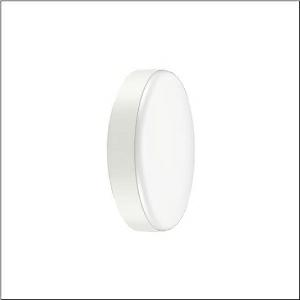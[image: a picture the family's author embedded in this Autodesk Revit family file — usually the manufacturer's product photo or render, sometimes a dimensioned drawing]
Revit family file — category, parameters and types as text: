
# Revit family: round_31_51wc10mb44as
name_source: partatom
category: Lighting Fixtures
units: mm (PartAtom-declared; Revit-internal decimal feet)

## family parameters
Cut with Voids When Loaded = No
Host = Face
Light Source = No
Part Type = Normal
Room Calculation Point = No
Round Connector Dimension = Use Diameter
Shared = No

## types (1)
- --- (1 x LED, 4400 lm, 35.5 W, 4000K)
    Apparent Load = 36 VA
    CIE Flux Codes = 44 75 94 94 100
    Color Rendering = 80
    Color Temperature = 4000K
    Default Elevation = 1800 mm
    Description = Round 31, wall and ceiling luminaire, primary optical cover: cover, of PC, opal, light emission: direct distribution, primary light characteristic: symmetric, installation type: surface-mounted, LED, rated luminous flux: 4.400lm, luminous efficacy: 124lm/W, light colour: 840, colour temperature: 4000K, control gear: ON/OFF Multilumen, with terminal, 3-pole, max. 2.5mm², mains connection: 220..240V, AC, 50/60Hz, rated input power: 35.5W, luminaire housing, of PC, traffic white (RAL 9016), diameter: 480mm, brightness and presence sensor, HF sensor, protection rating (complete): IP65, insulation class (complete): insulation class II (safety insulation), certification: CE, impact resistance: IK10, permissible operating ambient temperature: -20..+40°C, permissible storage temperature: -20..+60°C, packaging unit: 1 piece
    Height = 97 mm
    Lamp = 1 x LED
    Lamp Light Flux = 4400 lm
    Lamp Power = 35.5 W
    Lamp count = 1
    Length = 480 mm
    Luminous efficacy = 124 lm/W
    Manufacturer = Siteco
    ModVariant = No
    Model = 51WC10MB44AS
    Mounting Place = Ceiling
    Mounting Type = Surface mounted
    Number of Poles = 1
    OnlyDefault = Yes
    Power Factor = 1
    Product Name = Round 31
    Product group = wall and ceiling luminaire
    ProductGroupID = 304
    Protection Class = Protection class II
    Protection Degree = IP 65
    RLX_Detail_Level = 1
    RLX_Emergency_Light_Flux = 0 lm
    RLX_Emergency_Type = 0
    RLX_Emergency_Type_DB = No
    RlxData = <blob elided: 41469 chars, md5=67436c52>
    Socket = socket
    Standby Power = 0 W
    System Light Flux = 4400 lm
    System Power = 36 W
    Type Comments = factory setting: luminous flux: 100 % | (ON | ON)
    Type Image = l_1007188.jpg
    URL = http://relux.com
    VarID = @adj_150832
    Voltage = 0 V
    Weight = 0.00 kg
    Width = 0 mm  [stored 0 ft]

note: [stored X ft] marks values corroborated as IEEE doubles in the binary element streams (Revit-internal decimal feet)

## geometry (parser evidence)
native form markers: Blend x4, Sweep x14
no freeform markers — native parametric forms only
